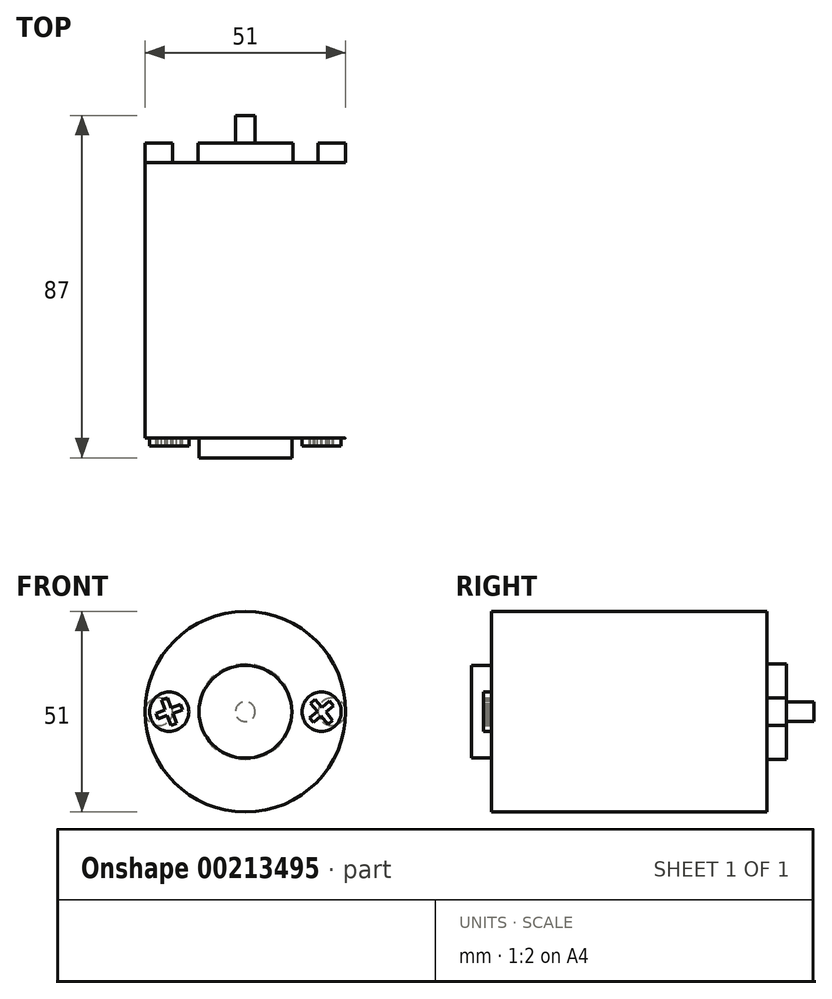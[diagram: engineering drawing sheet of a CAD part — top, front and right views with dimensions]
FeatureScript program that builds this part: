
annotation { "Feature Type Name" : "Feature", "Feature Type Description" : "" }
export const myFeature = defineFeature(function(context is Context, id is Id, definition is map)
    precondition{}
    {
        {
            var Q0;
            Q0=qCreatedBy(makeId("Front.planeOp"),FACE);
            var sketch = newSketch(context, id + "F0", { "sketchPlane" : qUnion([Q0])});
            skCircle(sketch, "E0", {"center": v(0, 0) * mm, "radius": 25.5 * mm});
            skSolve(sketch);
        }
        {
            var Q0;
            Q0 = qSketchRegion(id + "F0", true);
            extrude(context, id + "F1", {"entities" : qUnion([Q0]), "depth" : 70 * mm});
        }
        {
            var Q0;
            Q0=makeQuery(id+"F1.opExtrude","CAP_FACE",FACE,{"disambiguationData":[OSD([sQuery(id+"F0.wireOp",EDGE,"E0")])],"isStart":false});
            var sketch = newSketch(context, id + "F2", { "sketchPlane" : qUnion([Q0])});
            skCircle(sketch, "E1", {"center": v(0, 0) * mm, "radius": 11.8 * mm});
            skSolve(sketch);
        }
        {
            var Q0;
            Q0 = qSketchRegion(id + "F2", true);
            extrude(context, id + "F3", {"entities" : qUnion([Q0]), "operationType" : NewBodyOperationType.ADD, "depth" : 5 * mm});
        }
        {
            var Q0;
            Q0=makeQuery(id+"F1.opExtrude","CAP_FACE",FACE,{"disambiguationData":[OSD([sQuery(id+"F0.wireOp",EDGE,"E0")])],"isStart":true});
            var sketch = newSketch(context, id + "F4", { "sketchPlane" : qUnion([Q0])});
            skCircle(sketch, "E2", {"center": v(0, 0) * mm, "radius": 12.08 * mm});
            skLineSegment(sketch, "E3", {"start": v(0, 0) * mm, "end": v(-22, 0) * mm, "construction": true});
            skLineSegment(sketch, "E4", {"start": v(0, 0) * mm, "end": v(0, -18.21) * mm, "construction": true});
            skCircle(sketch, "E5", {"center": v(-22, 0) * mm, "radius": 3.5 * mm});
            skCircle(sketch, "E6.MirrorC", {"center": v(22, 0) * mm, "radius": 3.5 * mm});
            skSolve(sketch);
        }
        {
            var Q0;
            Q0 = qSketchRegion(id + "F4", true);
            extrude(context, id + "F5", {"entities" : qUnion([Q0]), "operationType" : NewBodyOperationType.ADD, "depth" : 5 * mm});
        }
        {
            var Q0;
            Q0=makeQuery(id+"F5.opExtrude","CAP_FACE",FACE,{"disambiguationData":[OSD([sQuery(id+"F4.wireOp",EDGE,"E2")])],"isStart":false});
            var sketch = newSketch(context, id + "F6", { "sketchPlane" : qUnion([Q0])});
            skCircle(sketch, "E7", {"center": v(0, 0) * mm, "radius": 2.5 * mm});
            skSolve(sketch);
        }
        {
            var Q0;
            Q0 = qSketchRegion(id + "F6", true);
            extrude(context, id + "F7", {"entities" : qUnion([Q0]), "operationType" : NewBodyOperationType.ADD, "depth" : 7 * mm});
        }
        {
            var Q0;
            Q0=makeQuery(id+"F1.opExtrude","CAP_FACE",FACE,{"disambiguationData":[OSD([sQuery(id+"F0.wireOp",EDGE,"E0")])],"isStart":false});
            var sketch = newSketch(context, id + "F8", { "sketchPlane" : qUnion([Q0])});
            skLineSegment(sketch, "E8", {"start": v(0, 17.93) * mm, "end": v(0, 0) * mm, "construction": true});
            skCircle(sketch, "E9", {"center": v(-19.36, 0) * mm, "radius": 5 * mm});
            skLineSegment(sketch, "E10.bottom", {"start": v(-21.3, 3) * mm, "end": v(-19.8, 3.54) * mm});
            skLineSegment(sketch, "E10.top", {"start": v(-18.91, -3.54) * mm, "end": v(-17.43, -3) * mm});
            skLineSegment(sketch, "E10.left", {"start": v(-21.3, 3) * mm, "end": v(-20.36, 0.44) * mm});
            skLineSegment(sketch, "E10.right", {"start": v(-19.8, 3.54) * mm, "end": v(-18.88, 0.98) * mm});
            skLineSegment(sketch, "E11.bottom", {"start": v(-22.2, -1.83) * mm, "end": v(-19.84, -0.98) * mm});
            skLineSegment(sketch, "E11.top", {"start": v(-22.7, -0.41) * mm, "end": v(-20.36, 0.44) * mm});
            skLineSegment(sketch, "E11.left", {"start": v(-22.2, -1.83) * mm, "end": v(-22.7, -0.41) * mm});
            skLineSegment(sketch, "E11.right", {"start": v(-16.01, 0.41) * mm, "end": v(-16.53, 1.83) * mm});
            skLineSegment(sketch, "E12.trimOffspring", {"start": v(-18.88, 0.98) * mm, "end": v(-16.53, 1.83) * mm});
            skLineSegment(sketch, "E13.trimOffspring", {"start": v(-18.36, -0.44) * mm, "end": v(-17.43, -3) * mm});
            skLineSegment(sketch, "E14.trimOffspring", {"start": v(-18.36, -0.44) * mm, "end": v(-16.01, 0.41) * mm});
            skLineSegment(sketch, "E15.trimOffspring", {"start": v(-19.84, -0.98) * mm, "end": v(-18.91, -3.54) * mm});
            skLineSegment(sketch, "E16.MirrorCS", {"start": v(17.33, -2.7) * mm, "end": v(16.36, -1.53) * mm});
            skLineSegment(sketch, "E17.MirrorCS", {"start": v(22.36, 1.53) * mm, "end": v(21.4, 2.7) * mm});
            skLineSegment(sketch, "E18.MirrorCS", {"start": v(22.2, -2.16) * mm, "end": v(21, -3.17) * mm});
            skLineSegment(sketch, "E19.MirrorCS", {"start": v(17.73, 3.17) * mm, "end": v(16.52, 2.16) * mm});
            skPoint(sketch, "E20.MirrorP", {"position": v(19.36, 0) * mm});
            skLineSegment(sketch, "E21.MirrorCS", {"start": v(18.27, 0.07) * mm, "end": v(16.36, -1.53) * mm});
            skLineSegment(sketch, "E22.MirrorCS", {"start": v(21.4, 2.7) * mm, "end": v(19.48, 1.08) * mm});
            skLineSegment(sketch, "E23.MirrorCS", {"start": v(19.24, -1.08) * mm, "end": v(21, -3.17) * mm});
            skLineSegment(sketch, "E24.MirrorCS", {"start": v(19.24, -1.08) * mm, "end": v(17.33, -2.7) * mm});
            skLineSegment(sketch, "E25.MirrorCS", {"start": v(20.45, -0.07) * mm, "end": v(22.2, -2.16) * mm});
            skLineSegment(sketch, "E26.MirrorCS", {"start": v(22.36, 1.53) * mm, "end": v(20.45, -0.07) * mm});
            skLineSegment(sketch, "E27.MirrorCS", {"start": v(16.52, 2.16) * mm, "end": v(18.27, 0.07) * mm});
            skLineSegment(sketch, "E28.MirrorCS", {"start": v(17.73, 3.17) * mm, "end": v(19.48, 1.08) * mm});
            skCircle(sketch, "E29.MirrorC", {"center": v(19.36, 0) * mm, "radius": 5 * mm});
            skSolve(sketch);
        }
        {
            var Q0;
            Q0 = qSketchRegion(id + "F8", true);
            extrude(context, id + "F9", {"entities" : qUnion([Q0]), "operationType" : NewBodyOperationType.ADD, "depth" : 2 * mm});
        }
    });
